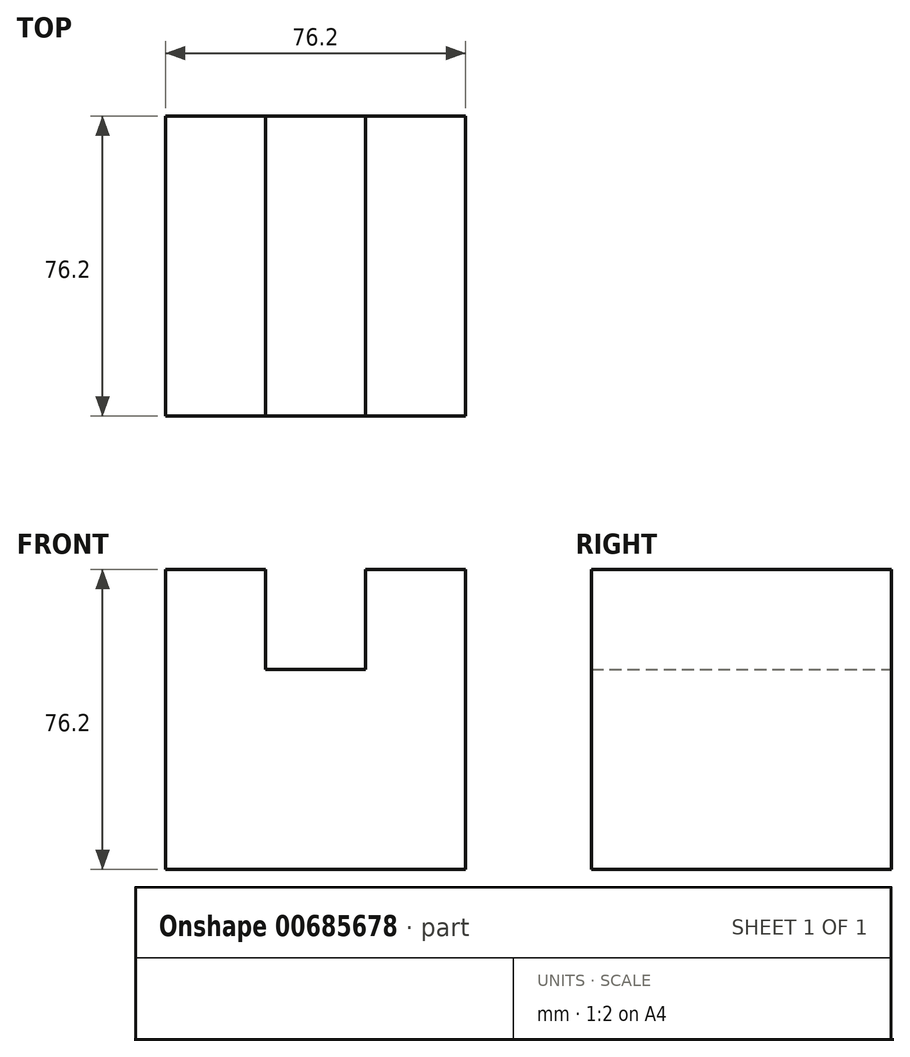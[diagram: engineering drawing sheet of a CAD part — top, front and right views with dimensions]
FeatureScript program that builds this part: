
annotation { "Feature Type Name" : "Feature", "Feature Type Description" : "" }
export const myFeature = defineFeature(function(context is Context, id is Id, definition is map)
    precondition{}
    {
        {
            var Q0;
            Q0=qCreatedBy(makeId("Front.planeOp"),FACE);
            var sketch = newSketch(context, id + "F0", { "sketchPlane" : qUnion([Q0])});
            skLineSegment(sketch, "E0", {"start": v(-43.1, -22.46) * mm, "end": v(-43.1, 53.74) * mm});
            skLineSegment(sketch, "E1", {"start": v(-43.1, 53.74) * mm, "end": v(-17.7, 53.74) * mm});
            skLineSegment(sketch, "E2", {"start": v(-17.7, 53.74) * mm, "end": v(-17.7, 28.34) * mm});
            skLineSegment(sketch, "E3", {"start": v(-17.7, 28.34) * mm, "end": v(7.7, 28.34) * mm});
            skLineSegment(sketch, "E4", {"start": v(7.7, 28.34) * mm, "end": v(7.7, 53.74) * mm});
            skLineSegment(sketch, "E5", {"start": v(7.7, 53.74) * mm, "end": v(33.1, 53.74) * mm});
            skLineSegment(sketch, "E6", {"start": v(33.1, 53.74) * mm, "end": v(33.1, -22.46) * mm});
            skLineSegment(sketch, "E7", {"start": v(33.1, -22.46) * mm, "end": v(-43.1, -22.46) * mm});
            skSolve(sketch);
        }
        {
            var Q0;
            Q0 = qSketchRegion(id + "F0", true);
            extrude(context, id + "F1", {"entities" : qUnion([Q0]), "depth" : 76.2 * mm, "offsetDistance" : 25.4 * mm});
        }
    });
